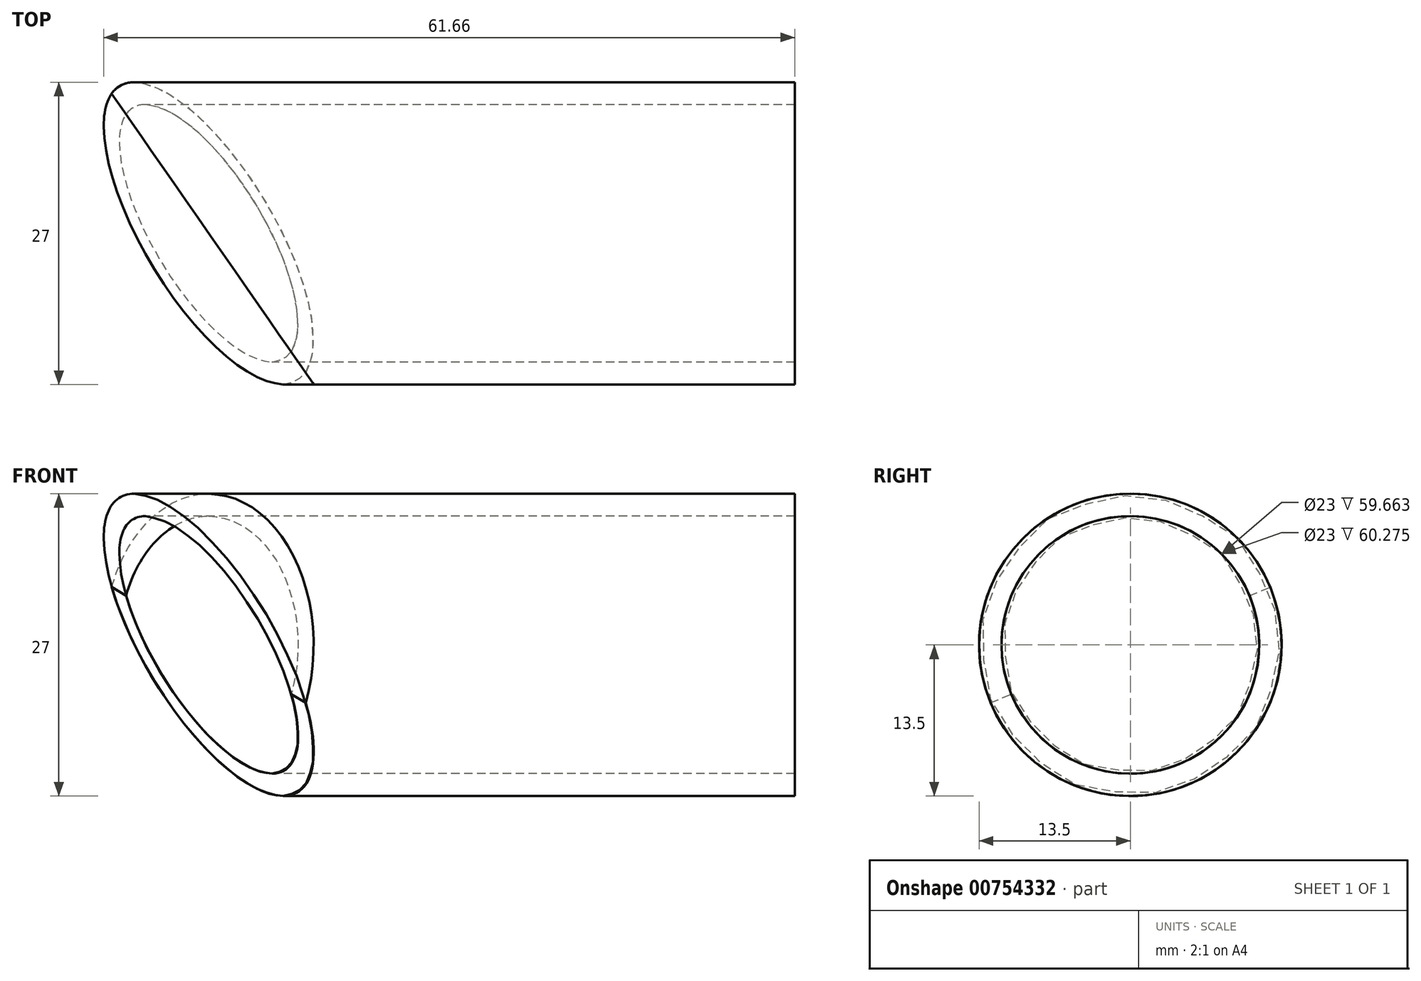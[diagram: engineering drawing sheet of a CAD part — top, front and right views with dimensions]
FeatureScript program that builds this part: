
annotation { "Feature Type Name" : "Feature", "Feature Type Description" : "" }
export const myFeature = defineFeature(function(context is Context, id is Id, definition is map)
    precondition{}
    {
        {
            var Q0;
            Q0=qCreatedBy(makeId("Right.planeOp"),FACE);
            var sketch = newSketch(context, id + "F0", { "sketchPlane" : qUnion([Q0])});
            skCircle(sketch, "E0", {"center": v(0, 0) * mm, "radius": 13.5 * mm});
            skCircle(sketch, "E1", {"center": v(0, 0) * mm, "radius": 11.5 * mm});
            skSolve(sketch);
        }
        {
            var Q0;
            Q0 = qSketchRegion(id + "F0", true);
            extrude(context, id + "F1", {"entities" : qUnion([Q0]), "depth" : 61.66 * mm, "offsetDistance" : 25 * mm});
        }
        {
            var Q0;
            Q0=qCreatedBy(makeId("Top.planeOp"),FACE);
            var sketch = newSketch(context, id + "F2", { "sketchPlane" : qUnion([Q0])});
            skLineSegment(sketch, "E2", {"start": v(0, 13.5) * mm, "end": v(18.75, -13.5) * mm});
            skLineSegment(sketch, "E3", {"start": v(18.75, -13.5) * mm, "end": v(0, -13.5) * mm});
            skLineSegment(sketch, "E4", {"start": v(0, -13.5) * mm, "end": v(0, 13.5) * mm});
            skLineSegment(sketch, "E5", {"start": v(0, 0) * mm, "end": v(0, 13.5) * mm, "construction": true});
            skSolve(sketch);
        }
        {
            var Q0;
            Q0 = qSketchRegion(id + "F2", true);
            extrude(context, id + "F3", {"entities" : qUnion([Q0]), "operationType" : NewBodyOperationType.REMOVE, "depth" : 25 * mm, "offsetDistance" : 25 * mm, "hasSecondDirection" : true, "secondDirectionOppositeDirection" : true, "secondDirectionDepth" : 25 * mm});
        }
        {
            var Q0;
            Q0=makeQuery(id+"F1.opExtrude","SWEPT_BODY",BODY,{"disambiguationData":[OSD([sQuery(id+"F0.wireOp",EDGE,"E0"),sQuery(id+"F0.wireOp",EDGE,"E1")])]});
            var Q1;
            Q1=makeQuery(id+"F1.opExtrude","SWEPT_FACE",FACE,{"disambiguationData":[OSD([sQuery(id+"F0.wireOp",EDGE,"E1")])]});
            transform(context, id + "F4", {"entities" : qUnion([Q0]), "transformType" : TransformType.ROTATION, "transformAxis" : qUnion([Q1]), "angle" : 45 * degree, "makeCopy" : false});
        }
    });
